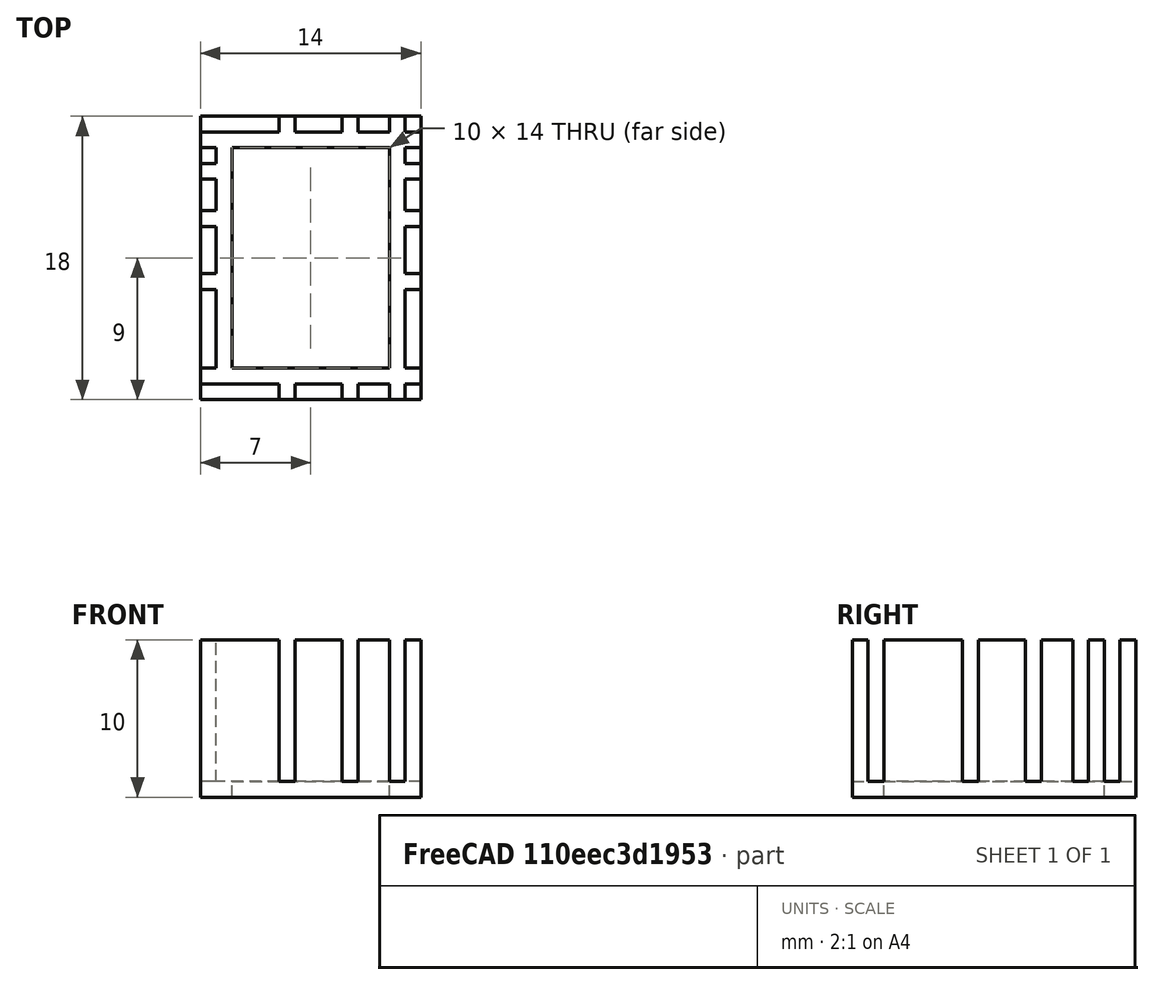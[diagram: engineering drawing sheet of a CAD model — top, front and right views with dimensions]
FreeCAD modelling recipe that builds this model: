
FCSTD DOCUMENT  (FreeCAD 0.18R16146 (Git))
Label: short-segment-calibration
License: All rights reserved
LicenseURL: http://en.wikipedia.org/wiki/All_rights_reserved
objects: Part::Box×6, Part::Feature×3, Part::MultiFuse×2, Part::Cut×1
note: 12 computed .brp shape members not serialized (recipe doc carries the construction recipe); baked Part::Feature solids carry a one-line shape summary decoded from their .brp

FEATURE [Part::Box] Box  label="Cube"
  AttacherType = Attacher::AttachEngine3D
  Height = 1
  Length = 14
  Width = 18
FEATURE [Part::Box] Box001  label="Cube001"
  AttacherType = Attacher::AttachEngine3D
  Height = 10
  Length = 5
  Width = 1
FEATURE [Part::Box] Box002  label="Cube002"
  AttacherType = Attacher::AttachEngine3D
  Height = 10
  Length = 3
  Placement = pos=(6,0,0) rot=(0,0,1;0rad)
  Width = 1
FEATURE [Part::Box] Box003  label="Cube003"
  AttacherType = Attacher::AttachEngine3D
  Height = 10
  Length = 2
  Placement = pos=(10,0,0) rot=(0,0,1;0rad)
  Width = 1
FEATURE [Part::Box] Box004  label="Cube004"
  AttacherType = Attacher::AttachEngine3D
  Height = 10
  Length = 1
  Placement = pos=(13,0,0) rot=(0,0,1;0rad)
  Width = 1
FEATURE [Part::MultiFuse] Fusion
  Shapes = -> [Box001,Box003,Box002,Box004]
FEATURE [Part::Feature] Fusion001
  Placement = pos=(1,2,0) rot=(0,0,1;1.5708rad)
  shape: bbox 1 x 14 x 10 mm, 24 faces, 4 solids (baked)
FEATURE [Part::Feature] Fusion002
  Placement = pos=(8.4e-15,17,0) rot=(0,0,1;0rad)
  shape: bbox 14 x 1 x 10 mm, 24 faces, 4 solids (baked)
FEATURE [Part::Feature] Fusion003
  Placement = pos=(14,2,0) rot=(0,0,1;1.5708rad)
  shape: bbox 1 x 14 x 10 mm, 24 faces, 4 solids (baked)
FEATURE [Part::Box] Box005  label="Cube005"
  AttacherType = Attacher::AttachEngine3D
  Height = 1
  Length = 10
  Placement = pos=(2,2,0) rot=(0,0,1;0rad)
  Width = 14
FEATURE [Part::Cut] Cut
  Base = -> Box
  Tool = -> Box005
FEATURE [Part::MultiFuse] Fusion004
  Shapes = -> [Cut,Fusion001,Fusion002,Fusion003,Fusion]
